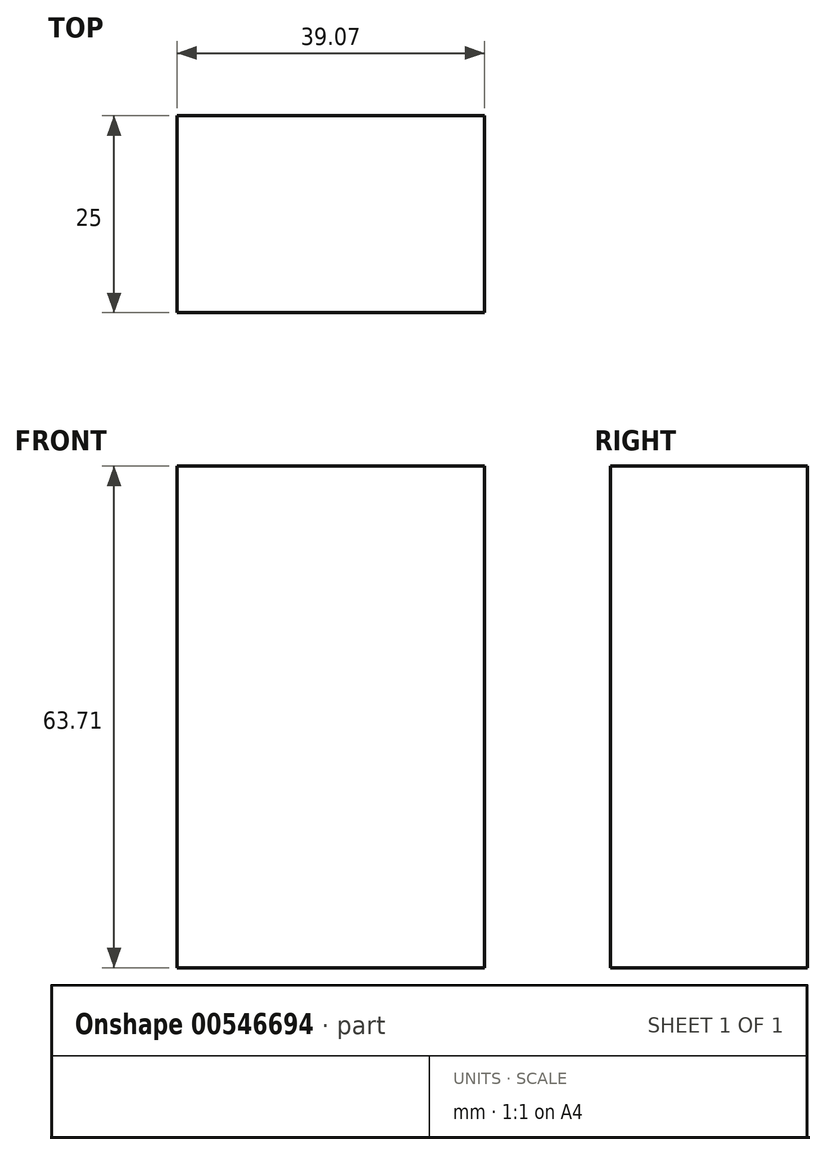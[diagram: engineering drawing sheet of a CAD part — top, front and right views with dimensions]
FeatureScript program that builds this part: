
annotation { "Feature Type Name" : "Feature", "Feature Type Description" : "" }
export const myFeature = defineFeature(function(context is Context, id is Id, definition is map)
    precondition{}
    {
        {
            var Q0;
            Q0=qCreatedBy(makeId("Front.planeOp"),FACE);
            var sketch = newSketch(context, id + "F0", { "sketchPlane" : qUnion([Q0])});
            skLineSegment(sketch, "E0.bottom", {"start": v(-93.53, 38.58) * mm, "end": v(-54.46, 38.58) * mm});
            skLineSegment(sketch, "E0.top", {"start": v(-93.53, -25.13) * mm, "end": v(-54.46, -25.13) * mm});
            skLineSegment(sketch, "E0.left", {"start": v(-93.53, 38.58) * mm, "end": v(-93.53, -25.13) * mm});
            skLineSegment(sketch, "E0.right", {"start": v(-54.46, 38.58) * mm, "end": v(-54.46, -25.13) * mm});
            skSolve(sketch);
        }
        {
            var Q0;
            Q0 = qSketchRegion(id + "F0", true);
            extrude(context, id + "F1", {"entities" : qUnion([Q0]), "depth" : 25 * mm, "offsetDistance" : 25 * mm});
        }
    });
